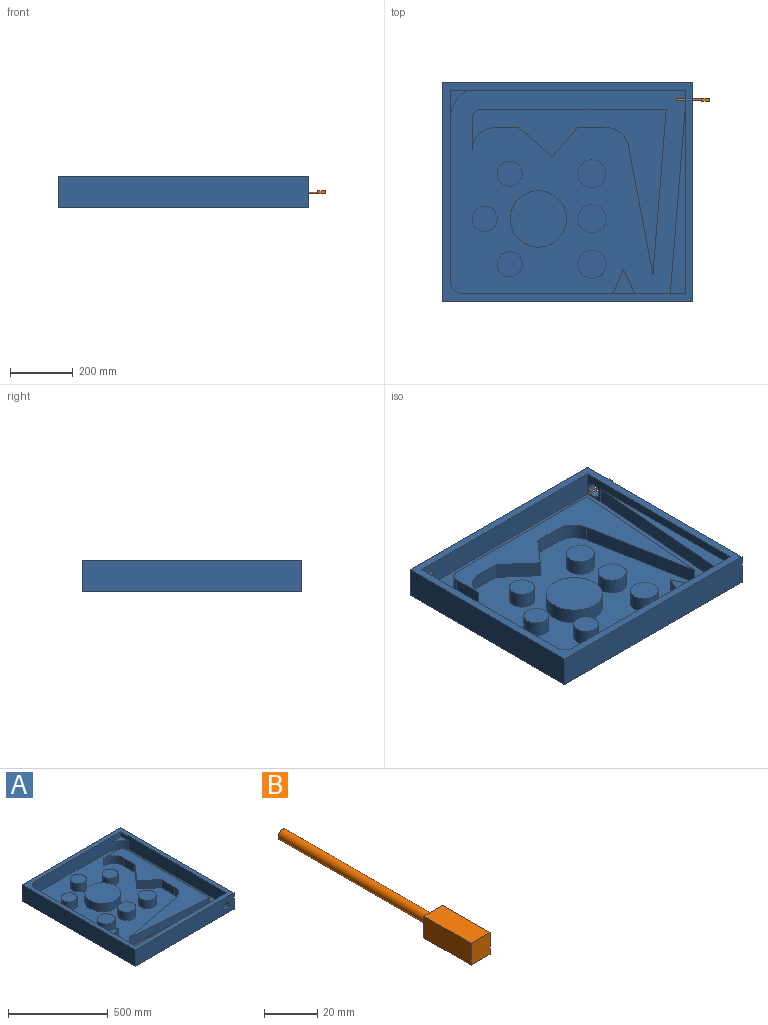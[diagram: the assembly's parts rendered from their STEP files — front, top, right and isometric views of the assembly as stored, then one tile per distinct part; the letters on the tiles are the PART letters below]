
ASSEMBLY  parts=2 mates=1
PART A: 46 faces, bbox 700x800x100 mm
  f0: plane 750x650mm, normal (0,0,1), area 332235.3mm2, adj f1,f2,f3,f4,f11,f12,f13,f14
  f1: plane 710x80mm, normal (1,0,0), area 50944.3mm2, adj f0,f4,f5,f12,f22,f23,f43,f44
  f2: plane 79.22x50mm, normal (-1,0,0), area 3961.1mm2, adj f0,f16,f21,f41
  f3: plane 750x80mm, normal (-1,0,0), area 57179.4mm2, adj f0,f4,f5,f11,f24,f25
  f4: plane 650x80mm, normal (0,1,0), area 20909.6mm2, adj f0,f1,f3,f5,f22,f23,f26
  f5: plane 800x700mm, normal (0,0,1), area 72843.4mm2, adj f1,f3,f4,f6,f7,f8,f9,f11
  f6: plane 700x100mm, normal (0,1,0), area 70000mm2, adj f5,f7,f9,f10
  f7: plane 800x100mm, normal (-1,0,0), area 80000mm2, adj f5,f6,f8,f10
  f8: plane 700x100mm, normal (0,-1,0), area 68409.6mm2, adj f5,f7,f9,f10,f26
  f9: plane 800x100mm, normal (1,0,0), area 80000mm2, adj f5,f6,f8,f10
  f10: plane 800x700mm, normal (0,0,-1), area 560000mm2, adj f6,f7,f8,f9
  f11: plane 610x80mm, normal (0,-1,0), area 44300mm2, adj f0,f3,f5,f12,f24,f25
  f12: cylinder r=40mm len=80mm, axis (0,0,1), area 5026.5mm2, adj f0,f1,f5,f11
  f13: plane 589.81x50mm, normal (1,0,0), area 29490.3mm2, adj f0,f14,f20,f21
  f14: cylinder r=30mm len=50mm, axis (0,0,-1), area 2411.6mm2, adj f0,f13,f15,f21
  f15: plane 98.89x50mm, normal (0,1,0), area 4944.6mm2, adj f0,f14,f16,f21
  f16: cylinder r=70mm len=70mm, axis (0,0,-1), area 5497.8mm2, adj f0,f2,f15,f21
  f17: plane 92.94x50mm, normal (-1,0,0), area 4646.9mm2, adj f0,f18,f21,f42
  f18: cylinder r=70mm len=68.77mm, axis (0,0,-1), area 4840.7mm2, adj f0,f17,f19,f21
  f19: plane 413.06x78.47mm, normal (-0.19,0.98,0), area 21022.6mm2, adj f0,f18,f20,f21
  f20: plane 530x50mm, normal (-0.08,-1,0), area 26585.5mm2, adj f0,f13,f19,f21
  f21: plane 619.81x530mm, normal (0,0,1), area 77167.9mm2, adj f2,f13,f14,f15,f16,f17,f18,f19
  f22: plane 590x50mm, normal (0.08,1,0), area 29595.2mm2, adj f0,f1,f4,f23
  f23: plane 590x47.45mm, normal (0,0,1), area 13996.2mm2, adj f1,f4,f22
  f24: cylinder r=100mm len=90mm, axis (0,0,-1), area 5598.8mm2, adj f0,f3,f11,f25
  f25: plane 90x56.41mm, normal (0,0,1), area 1439.6mm2, adj f3,f11,f24
  f26: cylinder r=22.5mm len=45mm, axis (0,1,0), area 3534.3mm2, adj f4,f8
  f27: cylinder r=90mm len=180mm, axis (0,0,-1), area 28274.3mm2, adj f0,f28
  f28: plane 180x180mm, normal (0,0,1), area 25446.9mm2, adj f27
  f29: cylinder r=40mm len=80mm, axis (0,0,-1), area 12566.4mm2, adj f0,f30
  f30: plane 80x80mm, normal (0,0,1), area 5026.5mm2, adj f29
  f31: cylinder r=40mm len=80mm, axis (0,0,-1), area 12566.4mm2, adj f0,f32
  f32: plane 80x80mm, normal (0,0,1), area 5026.5mm2, adj f31
  f33: cylinder r=40mm len=80mm, axis (0,0,-1), area 12566.4mm2, adj f0,f34
  f34: plane 80x80mm, normal (0,0,1), area 5026.5mm2, adj f33
  f35: cylinder r=45mm len=90mm, axis (0,0,-1), area 14137.2mm2, adj f0,f36
  f36: plane 90x90mm, normal (0,0,1), area 6361.7mm2, adj f35
  f37: cylinder r=45mm len=90mm, axis (0,0,-1), area 14137.2mm2, adj f0,f38
  f38: plane 90x90mm, normal (0,0,1), area 6361.7mm2, adj f37
  f39: cylinder r=45mm len=90mm, axis (0,0,-1), area 14137.2mm2, adj f0,f40
  f40: plane 90x90mm, normal (0,0,1), area 6361.7mm2, adj f39
  f41: plane 106.49x93.03mm, normal (-0.75,0.66,0), area 7070.3mm2, adj f0,f2,f21,f42
  f42: plane 93.03x81.27mm, normal (-0.66,-0.75,0), area 6176.7mm2, adj f0,f17,f21,f41
  f43: plane 77.68x50mm, normal (0.39,0.92,0), area 4216.8mm2, adj f0,f1,f44,f45
  f44: plane 77.68x50mm, normal (0.43,-0.9,0), area 4298.2mm2, adj f0,f1,f43,f45
  f45: plane 77.68x69.67mm, normal (0,0,1), area 2705.8mm2, adj f1,f43,f44
PART B: 8 faces, bbox 10x105x10 mm
  f0: cylinder r=2.25mm len=80mm, axis (0,1,0), area 1131mm2, adj f1,f7
  f1: plane 4.5x4.5mm, normal (0,1,0), area 15.9mm2, adj f0
  f2: plane 25x10mm, normal (0,0,-1), area 250mm2, adj f3,f5,f6,f7
  f3: plane 25x10mm, normal (1,0,0), area 250mm2, adj f2,f4,f6,f7
  f4: plane 25x10mm, normal (0,0,1), area 250mm2, adj f3,f5,f6,f7
  f5: plane 25x10mm, normal (-1,0,0), area 250mm2, adj f2,f4,f6,f7
  f6: plane 10x10mm, normal (0,-1,0), area 100mm2, adj f2,f3,f4,f5
  f7: plane 10x10mm, normal (0,1,0), area 84.1mm2, adj f0,f2,f3,f4,f5
PLACE A rot(axis=(0,0,1),90deg) t=(-400,350,100)mm
PLACE B rot(axis=(0,0,1),90deg) t=(-52.12,218.22,121.17)mm
MATE slider B.f0 <-> A.f26  axis (-1,0,0) through (-52.12,645,49)mm
